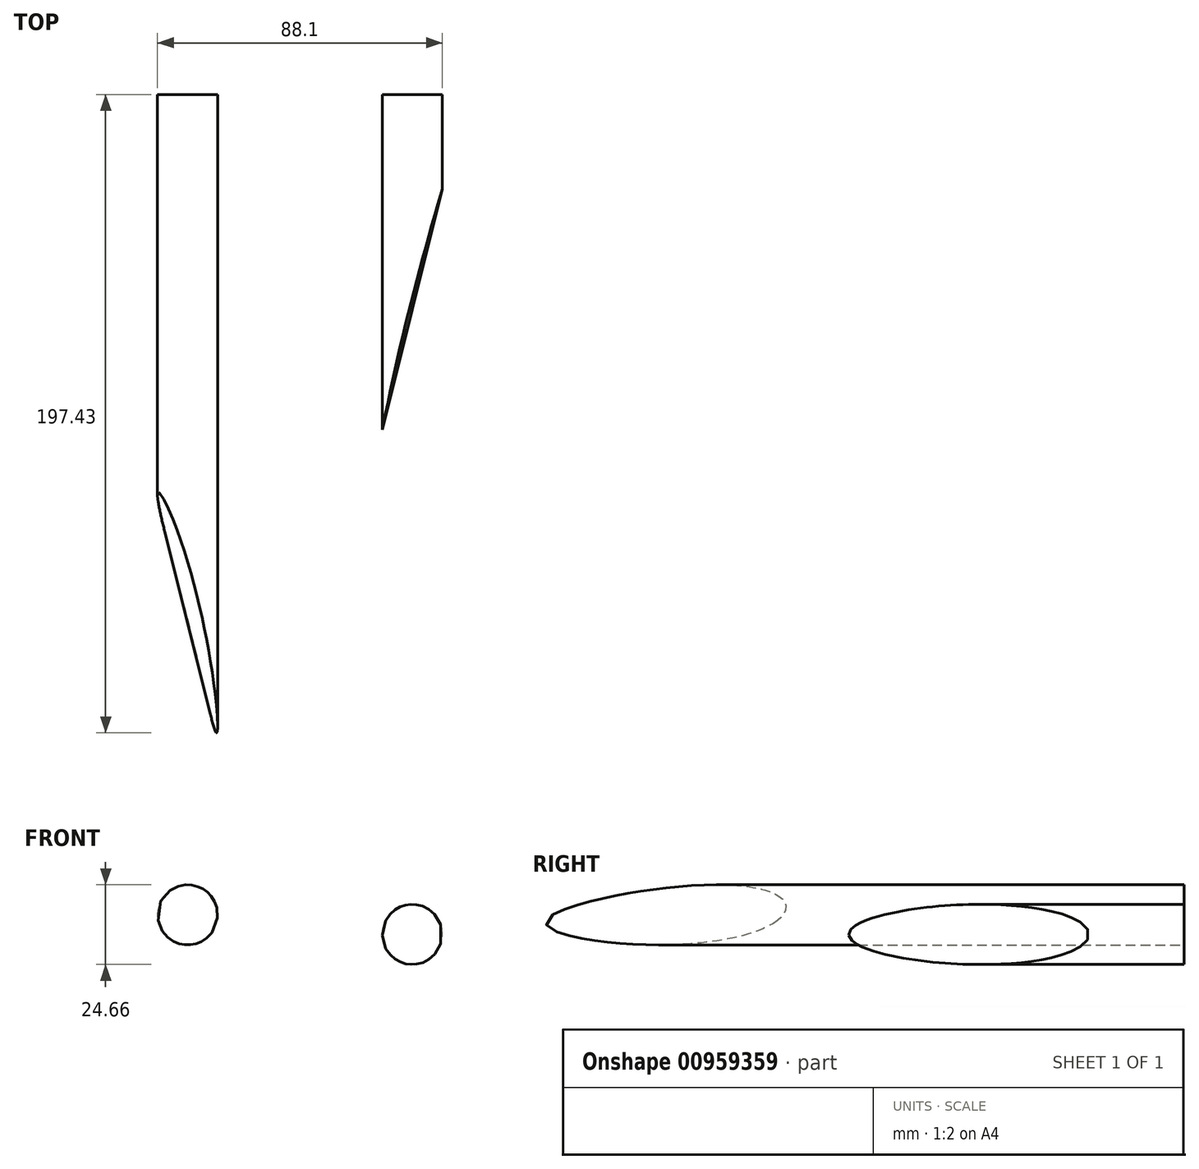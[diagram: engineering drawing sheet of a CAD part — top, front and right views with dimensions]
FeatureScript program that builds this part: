
annotation { "Feature Type Name" : "Feature", "Feature Type Description" : "" }
export const myFeature = defineFeature(function(context is Context, id is Id, definition is map)
    precondition{}
    {
        {
            var Q0;
            Q0=qCreatedBy(makeId("Front.planeOp"),FACE);
            var sketch = newSketch(context, id + "F0", { "sketchPlane" : qUnion([Q0])});
            skCircle(sketch, "E0", {"center": v(0, 0) * mm, "radius": 63.5 * mm});
            skLineSegment(sketch, "E1.0", {"start": v(40.6, 23.44) * mm, "end": v(40.6, -23.44) * mm, "construction": true});
            skLineSegment(sketch, "E1.1", {"start": v(40.6, -23.44) * mm, "end": v(0, -46.87) * mm, "construction": true});
            skLineSegment(sketch, "E1.2", {"start": v(0, -46.87) * mm, "end": v(-40.6, -23.44) * mm, "construction": true});
            skLineSegment(sketch, "E1.3", {"start": v(-40.6, -23.44) * mm, "end": v(-40.6, 23.44) * mm, "construction": true});
            skLineSegment(sketch, "E1.4", {"start": v(-40.6, 23.44) * mm, "end": v(0, 46.87) * mm, "construction": true});
            skLineSegment(sketch, "E1.5", {"start": v(0, 46.87) * mm, "end": v(40.6, 23.44) * mm, "construction": true});
            skPoint(sketch, "E1.0.midPoint", {"position": v(40.6, 0) * mm});
            skCircle(sketch, "E2", {"center": v(0, 0) * mm, "radius": 56.17 * mm, "construction": true});
            skCircle(sketch, "E3", {"center": v(0, 46.87) * mm, "radius": 9.3 * mm});
            skCircle(sketch, "E4", {"center": v(-40.6, 23.44) * mm, "radius": 9.3 * mm});
            skCircle(sketch, "E5", {"center": v(-40.6, -23.44) * mm, "radius": 9.3 * mm});
            skCircle(sketch, "E6", {"center": v(0, -46.87) * mm, "radius": 9.3 * mm});
            skCircle(sketch, "E7", {"center": v(40.6, -23.44) * mm, "radius": 9.3 * mm});
            skCircle(sketch, "E8", {"center": v(40.6, 23.44) * mm, "radius": 9.3 * mm});
            skCircle(sketch, "E9", {"center": v(-23.44, 40.6) * mm, "radius": 9.3 * mm});
            skCircle(sketch, "E10", {"center": v(-46.87, 0) * mm, "radius": 9.3 * mm});
            skCircle(sketch, "E11", {"center": v(-23.44, -40.6) * mm, "radius": 9.3 * mm});
            skLineSegment(sketch, "E12", {"start": v(-40.6, 23.44) * mm, "end": v(40.6, 23.44) * mm, "construction": true});
            skLineSegment(sketch, "E13", {"start": v(-40.6, -23.44) * mm, "end": v(40.6, -23.44) * mm, "construction": true});
            skCircle(sketch, "E14", {"center": v(23.44, 40.6) * mm, "radius": 9.3 * mm});
            skCircle(sketch, "E15", {"center": v(23.44, -40.6) * mm, "radius": 9.3 * mm});
            skCircle(sketch, "E16.MirrorC", {"center": v(46.87, 0) * mm, "radius": 9.3 * mm});
            skLineSegment(sketch, "E17", {"start": v(0, 0) * mm, "end": v(-28.09, 48.64) * mm});
            skLineSegment(sketch, "E18", {"start": v(0, 0) * mm, "end": v(28.09, -48.64) * mm});
            skLineSegment(sketch, "E19", {"start": v(0, 0) * mm, "end": v(-28.09, -48.64) * mm});
            skLineSegment(sketch, "E20", {"start": v(0, 0) * mm, "end": v(28.09, 48.64) * mm});
            skCircle(sketch, "E21", {"center": v(-22.64, 6.07) * mm, "radius": 9.3 * mm});
            skLineSegment(sketch, "E22.anchor1", {"start": v(0, 0) * mm, "end": v(-22.64, 6.07) * mm, "construction": true});
            skLineSegment(sketch, "E22.anchor2", {"start": v(0, 0) * mm, "end": v(-22.64, 6.07) * mm, "construction": true});
            skCircle(sketch, "E23.1.0", {"center": v(-16.57, -16.57) * mm, "radius": 9.3 * mm});
            skCircle(sketch, "E23.2.0", {"center": v(6.07, -22.64) * mm, "radius": 9.3 * mm});
            skCircle(sketch, "E24.1.3.0", {"center": v(22.64, -6.07) * mm, "radius": 9.3 * mm});
            skCircle(sketch, "E24.1.4.0", {"center": v(16.57, 16.57) * mm, "radius": 9.3 * mm});
            skCircle(sketch, "E24.1.5.0", {"center": v(-6.07, 22.64) * mm, "radius": 9.3 * mm});
            skSolve(sketch);
        }
        {
            var Q0;
            Q0=qCreatedBy(makeId("Right.planeOp"),FACE);
            var sketch = newSketch(context, id + "F1", { "sketchPlane" : qUnion([Q0])});
            skLineSegment(sketch, "E25", {"start": v(0, 0) * mm, "end": v(-254, 0) * mm});
            skLineSegment(sketch, "E26", {"start": v(0, 0) * mm, "end": v(0, 63.5) * mm});
            skLineSegment(sketch, "E27", {"start": v(-254, 0) * mm, "end": v(0, 63.5) * mm});
            skSolve(sketch);
        }
        {
            var Q0;
            Q0=makeQuery(id+"F1.imprint","IMPRINT",FACE,{"disambiguationData":[TD([[makeQuery(id+"F1.imprint","IMPRINT",EDGE,{"derivedFrom":sQuery(id+"F1.wireOp",EDGE,"E25")}),-1.0]])]});
            var Q1;
            Q1=sQuery(id+"F1.wireOp",EDGE,"E25");
            revolve(context, id + "F2", {"surfaceOperationType" : NewSurfaceOperationType.NEW, "entities" : qUnion([Q0]), "axis" : qUnion([Q1]), "revolveType" : RevolveType.FULL});
        }
        {
            var Q0;
            Q0=makeQuery(id+"F0.imprint","IMPRINT",FACE,{"disambiguationData":[TD([[makeQuery(id+"F0.imprint","IMPRINT",EDGE,{"derivedFrom":sQuery(id+"F0.wireOp",EDGE,"E10")}),1.0]])]});
            var Q1;
            Q1=makeQuery(id+"F0.imprint","IMPRINT",FACE,{"disambiguationData":[TD([[makeQuery(id+"F0.imprint","IMPRINT",EDGE,{"derivedFrom":sQuery(id+"F0.wireOp",EDGE,"E5")}),1.0]])]});
            var Q2;
            {var subQ0=sQuery(id+"F0.wireOp",EDGE,"E19");var subQ1=sQuery(id+"F0.wireOp",EDGE,"E11");var subQ2=makeQuery(id+"F0.imprint","INTERSECT",VERTEX,{"disambiguationData":[OD(0.0)],"derivedFrom":[subQ1,subQ0]});Q2=makeQuery(id+"F0.imprint","IMPRINT",FACE,{"disambiguationData":[TD([[makeQuery(id+"F0.imprint","IMPRINT",EDGE,{"disambiguationData":[TD([[subQ2,1.0]])],"derivedFrom":subQ1}),1.0]])]});}
            var Q3;
            {var subQ0=sQuery(id+"F0.wireOp",EDGE,"E19");var subQ1=sQuery(id+"F0.wireOp",EDGE,"E11");var subQ2=makeQuery(id+"F0.imprint","INTERSECT",VERTEX,{"disambiguationData":[OD(0.0)],"derivedFrom":[subQ1,subQ0]});Q3=makeQuery(id+"F0.imprint","IMPRINT",FACE,{"disambiguationData":[TD([[makeQuery(id+"F0.imprint","IMPRINT",EDGE,{"disambiguationData":[TD([[subQ2,-1.0]])],"derivedFrom":subQ1}),1.0]])]});}
            var Q4;
            Q4=makeQuery(id+"F0.imprint","IMPRINT",FACE,{"disambiguationData":[TD([[makeQuery(id+"F0.imprint","IMPRINT",EDGE,{"derivedFrom":sQuery(id+"F0.wireOp",EDGE,"E6")}),1.0]])]});
            var Q5;
            {var subQ0=sQuery(id+"F0.wireOp",EDGE,"E18");var subQ1=sQuery(id+"F0.wireOp",EDGE,"E15");var subQ2=makeQuery(id+"F0.imprint","INTERSECT",VERTEX,{"disambiguationData":[OD(0.0)],"derivedFrom":[subQ1,subQ0]});Q5=makeQuery(id+"F0.imprint","IMPRINT",FACE,{"disambiguationData":[TD([[makeQuery(id+"F0.imprint","IMPRINT",EDGE,{"disambiguationData":[TD([[subQ2,-1.0]])],"derivedFrom":subQ1}),1.0]])]});}
            var Q6;
            {var subQ0=sQuery(id+"F0.wireOp",EDGE,"E18");var subQ1=sQuery(id+"F0.wireOp",EDGE,"E15");var subQ2=makeQuery(id+"F0.imprint","INTERSECT",VERTEX,{"disambiguationData":[OD(0.0)],"derivedFrom":[subQ1,subQ0]});Q6=makeQuery(id+"F0.imprint","IMPRINT",FACE,{"disambiguationData":[TD([[makeQuery(id+"F0.imprint","IMPRINT",EDGE,{"disambiguationData":[TD([[subQ2,1.0]])],"derivedFrom":subQ1}),1.0]])]});}
            var Q7;
            Q7=makeQuery(id+"F0.imprint","IMPRINT",FACE,{"disambiguationData":[TD([[makeQuery(id+"F0.imprint","IMPRINT",EDGE,{"derivedFrom":sQuery(id+"F0.wireOp",EDGE,"E7")}),1.0]])]});
            var Q8;
            Q8=makeQuery(id+"F0.imprint","IMPRINT",FACE,{"disambiguationData":[TD([[makeQuery(id+"F0.imprint","IMPRINT",EDGE,{"derivedFrom":sQuery(id+"F0.wireOp",EDGE,"E16.MirrorC")}),-1.0]])]});
            var Q9;
            Q9=makeQuery(id+"F0.imprint","IMPRINT",FACE,{"disambiguationData":[TD([[makeQuery(id+"F0.imprint","IMPRINT",EDGE,{"derivedFrom":sQuery(id+"F0.wireOp",EDGE,"E8")}),1.0]])]});
            var Q10;
            {var subQ0=sQuery(id+"F0.wireOp",EDGE,"E20");var subQ1=sQuery(id+"F0.wireOp",EDGE,"E14");var subQ2=makeQuery(id+"F0.imprint","INTERSECT",VERTEX,{"disambiguationData":[OD(0.0)],"derivedFrom":[subQ1,subQ0]});Q10=makeQuery(id+"F0.imprint","IMPRINT",FACE,{"disambiguationData":[TD([[makeQuery(id+"F0.imprint","IMPRINT",EDGE,{"disambiguationData":[TD([[subQ2,1.0]])],"derivedFrom":subQ1}),1.0]])]});}
            var Q11;
            {var subQ0=sQuery(id+"F0.wireOp",EDGE,"E20");var subQ1=sQuery(id+"F0.wireOp",EDGE,"E14");var subQ2=makeQuery(id+"F0.imprint","INTERSECT",VERTEX,{"disambiguationData":[OD(0.0)],"derivedFrom":[subQ1,subQ0]});Q11=makeQuery(id+"F0.imprint","IMPRINT",FACE,{"disambiguationData":[TD([[makeQuery(id+"F0.imprint","IMPRINT",EDGE,{"disambiguationData":[TD([[subQ2,-1.0]])],"derivedFrom":subQ1}),1.0]])]});}
            var Q12;
            Q12=makeQuery(id+"F0.imprint","IMPRINT",FACE,{"disambiguationData":[TD([[makeQuery(id+"F0.imprint","IMPRINT",EDGE,{"derivedFrom":sQuery(id+"F0.wireOp",EDGE,"E3")}),1.0]])]});
            var Q13;
            {var subQ0=sQuery(id+"F0.wireOp",EDGE,"E17");var subQ1=sQuery(id+"F0.wireOp",EDGE,"E9");var subQ2=makeQuery(id+"F0.imprint","INTERSECT",VERTEX,{"disambiguationData":[OD(0.0)],"derivedFrom":[subQ1,subQ0]});Q13=makeQuery(id+"F0.imprint","IMPRINT",FACE,{"disambiguationData":[TD([[makeQuery(id+"F0.imprint","IMPRINT",EDGE,{"disambiguationData":[TD([[subQ2,-1.0]])],"derivedFrom":subQ1}),1.0]])]});}
            var Q14;
            {var subQ0=sQuery(id+"F0.wireOp",EDGE,"E17");var subQ1=sQuery(id+"F0.wireOp",EDGE,"E9");var subQ2=makeQuery(id+"F0.imprint","INTERSECT",VERTEX,{"disambiguationData":[OD(0.0)],"derivedFrom":[subQ1,subQ0]});Q14=makeQuery(id+"F0.imprint","IMPRINT",FACE,{"disambiguationData":[TD([[makeQuery(id+"F0.imprint","IMPRINT",EDGE,{"disambiguationData":[TD([[subQ2,1.0]])],"derivedFrom":subQ1}),1.0]])]});}
            var Q15;
            Q15=makeQuery(id+"F0.imprint","IMPRINT",FACE,{"disambiguationData":[TD([[makeQuery(id+"F0.imprint","IMPRINT",EDGE,{"derivedFrom":sQuery(id+"F0.wireOp",EDGE,"E4")}),1.0]])]});
            var Q16;
            Q16=makeQuery(id+"F0.imprint","IMPRINT",FACE,{"disambiguationData":[TD([[makeQuery(id+"F0.imprint","IMPRINT",EDGE,{"derivedFrom":sQuery(id+"F0.wireOp",EDGE,"E21")}),1.0]])]});
            var Q17;
            {var subQ0=sQuery(id+"F0.wireOp",EDGE,"E23.1.0");var subQ1=sQuery(id+"F0.wireOp",EDGE,"E19");var subQ2=makeQuery(id+"F0.imprint","INTERSECT",VERTEX,{"disambiguationData":[OD(0.0)],"derivedFrom":[subQ1,subQ0]});Q17=makeQuery(id+"F0.imprint","IMPRINT",FACE,{"disambiguationData":[TD([[makeQuery(id+"F0.imprint","IMPRINT",EDGE,{"disambiguationData":[TD([[subQ2,1.0]])],"derivedFrom":subQ1}),-1.0]])]});}
            var Q18;
            {var subQ0=sQuery(id+"F0.wireOp",EDGE,"E23.1.0");var subQ1=sQuery(id+"F0.wireOp",EDGE,"E19");var subQ2=makeQuery(id+"F0.imprint","INTERSECT",VERTEX,{"disambiguationData":[OD(0.0)],"derivedFrom":[subQ1,subQ0]});Q18=makeQuery(id+"F0.imprint","IMPRINT",FACE,{"disambiguationData":[TD([[makeQuery(id+"F0.imprint","IMPRINT",EDGE,{"disambiguationData":[TD([[subQ2,1.0]])],"derivedFrom":subQ1}),1.0]])]});}
            var Q19;
            {var subQ0=sQuery(id+"F0.wireOp",EDGE,"E23.2.0");var subQ1=sQuery(id+"F0.wireOp",EDGE,"E18");var subQ2=makeQuery(id+"F0.imprint","INTERSECT",VERTEX,{"disambiguationData":[OD(0.0)],"derivedFrom":[subQ1,subQ0]});Q19=makeQuery(id+"F0.imprint","IMPRINT",FACE,{"disambiguationData":[TD([[makeQuery(id+"F0.imprint","IMPRINT",EDGE,{"disambiguationData":[TD([[subQ2,-1.0]])],"derivedFrom":subQ1}),-1.0]])]});}
            var Q20;
            {var subQ0=sQuery(id+"F0.wireOp",EDGE,"E23.2.0");var subQ1=sQuery(id+"F0.wireOp",EDGE,"E18");var subQ2=makeQuery(id+"F0.imprint","INTERSECT",VERTEX,{"disambiguationData":[OD(0.0)],"derivedFrom":[subQ1,subQ0]});Q20=makeQuery(id+"F0.imprint","IMPRINT",FACE,{"disambiguationData":[TD([[makeQuery(id+"F0.imprint","IMPRINT",EDGE,{"disambiguationData":[TD([[subQ2,-1.0]])],"derivedFrom":subQ1}),1.0]])]});}
            var Q21;
            Q21=makeQuery(id+"F0.imprint","IMPRINT",FACE,{"disambiguationData":[TD([[makeQuery(id+"F0.imprint","IMPRINT",EDGE,{"derivedFrom":sQuery(id+"F0.wireOp",EDGE,"E24.1.3.0")}),1.0]])]});
            var Q22;
            {var subQ0=sQuery(id+"F0.wireOp",EDGE,"E24.1.4.0");var subQ1=sQuery(id+"F0.wireOp",EDGE,"E20");var subQ2=makeQuery(id+"F0.imprint","INTERSECT",VERTEX,{"disambiguationData":[OD(0.0)],"derivedFrom":[subQ1,subQ0]});Q22=makeQuery(id+"F0.imprint","IMPRINT",FACE,{"disambiguationData":[TD([[makeQuery(id+"F0.imprint","IMPRINT",EDGE,{"disambiguationData":[TD([[subQ2,-1.0]])],"derivedFrom":subQ1}),-1.0]])]});}
            var Q23;
            {var subQ0=sQuery(id+"F0.wireOp",EDGE,"E24.1.4.0");var subQ1=sQuery(id+"F0.wireOp",EDGE,"E20");var subQ2=makeQuery(id+"F0.imprint","INTERSECT",VERTEX,{"disambiguationData":[OD(0.0)],"derivedFrom":[subQ1,subQ0]});Q23=makeQuery(id+"F0.imprint","IMPRINT",FACE,{"disambiguationData":[TD([[makeQuery(id+"F0.imprint","IMPRINT",EDGE,{"disambiguationData":[TD([[subQ2,-1.0]])],"derivedFrom":subQ1}),1.0]])]});}
            var Q24;
            {var subQ0=sQuery(id+"F0.wireOp",EDGE,"E24.1.5.0");var subQ1=sQuery(id+"F0.wireOp",EDGE,"E17");var subQ2=makeQuery(id+"F0.imprint","INTERSECT",VERTEX,{"disambiguationData":[OD(0.0)],"derivedFrom":[subQ1,subQ0]});Q24=makeQuery(id+"F0.imprint","IMPRINT",FACE,{"disambiguationData":[TD([[makeQuery(id+"F0.imprint","IMPRINT",EDGE,{"disambiguationData":[TD([[subQ2,1.0]])],"derivedFrom":subQ1}),-1.0]])]});}
            var Q25;
            {var subQ0=sQuery(id+"F0.wireOp",EDGE,"E24.1.5.0");var subQ1=sQuery(id+"F0.wireOp",EDGE,"E17");var subQ2=makeQuery(id+"F0.imprint","INTERSECT",VERTEX,{"disambiguationData":[OD(0.0)],"derivedFrom":[subQ1,subQ0]});Q25=makeQuery(id+"F0.imprint","IMPRINT",FACE,{"disambiguationData":[TD([[makeQuery(id+"F0.imprint","IMPRINT",EDGE,{"disambiguationData":[TD([[subQ2,1.0]])],"derivedFrom":subQ1}),1.0]])]});}
            extrude(context, id + "F3", {"entities" : qUnion([Q0, Q1, Q2, Q3, Q4, Q5, Q6, Q7, Q8, Q9, Q10, Q11, Q12, Q13, Q14, Q15, Q16, Q17, Q18, Q19, Q20, Q21, Q22, Q23, Q24, Q25]), "depth" : 254 * mm, "offsetDistance" : 25.4 * mm});
        }
        {
            var Q0;
            Q0=makeQuery(id+"F3.opExtrude","SWEPT_BODY",BODY,{"disambiguationData":[OSD([sQuery(id+"F0.wireOp",EDGE,"E3")])]});
            var Q1;
            Q1=makeQuery(id+"F3.opExtrude","SWEPT_BODY",BODY,{"disambiguationData":[OSD([sQuery(id+"F0.wireOp",EDGE,"E24.1.4.0")])]});
            var Q2;
            Q2=makeQuery(id+"F3.opExtrude","SWEPT_BODY",BODY,{"disambiguationData":[OSD([sQuery(id+"F0.wireOp",EDGE,"E23.2.0")])]});
            var Q3;
            Q3=makeQuery(id+"F3.opExtrude","SWEPT_BODY",BODY,{"disambiguationData":[OSD([sQuery(id+"F0.wireOp",EDGE,"E21")])]});
            var Q4;
            Q4=makeQuery(id+"F3.opExtrude","SWEPT_BODY",BODY,{"disambiguationData":[OSD([sQuery(id+"F0.wireOp",EDGE,"E16.MirrorC")])]});
            var Q5;
            Q5=makeQuery(id+"F3.opExtrude","SWEPT_BODY",BODY,{"disambiguationData":[OSD([sQuery(id+"F0.wireOp",EDGE,"E11")])]});
            var Q6;
            Q6=makeQuery(id+"F3.opExtrude","SWEPT_BODY",BODY,{"disambiguationData":[OSD([sQuery(id+"F0.wireOp",EDGE,"E10")])]});
            var Q7;
            Q7=makeQuery(id+"F3.opExtrude","SWEPT_BODY",BODY,{"disambiguationData":[OSD([sQuery(id+"F0.wireOp",EDGE,"E9")])]});
            var Q8;
            Q8=makeQuery(id+"F3.opExtrude","SWEPT_BODY",BODY,{"disambiguationData":[OSD([sQuery(id+"F0.wireOp",EDGE,"E8")])]});
            var Q9;
            Q9=makeQuery(id+"F3.opExtrude","SWEPT_BODY",BODY,{"disambiguationData":[OSD([sQuery(id+"F0.wireOp",EDGE,"E7")])]});
            var Q10;
            Q10=makeQuery(id+"F3.opExtrude","SWEPT_BODY",BODY,{"disambiguationData":[OSD([sQuery(id+"F0.wireOp",EDGE,"E6")])]});
            var Q11;
            Q11=makeQuery(id+"F3.opExtrude","SWEPT_BODY",BODY,{"disambiguationData":[OSD([sQuery(id+"F0.wireOp",EDGE,"E5")])]});
            var Q12;
            Q12=makeQuery(id+"F3.opExtrude","SWEPT_BODY",BODY,{"disambiguationData":[OSD([sQuery(id+"F0.wireOp",EDGE,"E4")])]});
            var Q13;
            Q13=makeQuery(id+"F3.opExtrude","SWEPT_BODY",BODY,{"disambiguationData":[OSD([sQuery(id+"F0.wireOp",EDGE,"E15")])]});
            var Q14;
            Q14=makeQuery(id+"F3.opExtrude","SWEPT_BODY",BODY,{"disambiguationData":[OSD([sQuery(id+"F0.wireOp",EDGE,"E23.1.0")])]});
            var Q15;
            Q15=makeQuery(id+"F3.opExtrude","SWEPT_BODY",BODY,{"disambiguationData":[OSD([sQuery(id+"F0.wireOp",EDGE,"E24.1.3.0")])]});
            var Q16;
            Q16=makeQuery(id+"F3.opExtrude","SWEPT_BODY",BODY,{"disambiguationData":[OSD([sQuery(id+"F0.wireOp",EDGE,"E24.1.5.0")])]});
            var Q17;
            Q17=makeQuery(id+"F3.opExtrude","SWEPT_BODY",BODY,{"disambiguationData":[OSD([sQuery(id+"F0.wireOp",EDGE,"E14")])]});
            var Q18;
            Q18=makeQuery(id+"F2.opRevolve","SWEPT_BODY",BODY,{"disambiguationData":[OSD([sQuery(id+"F1.wireOp",EDGE,"E25"),sQuery(id+"F1.wireOp",EDGE,"E26"),sQuery(id+"F1.wireOp",EDGE,"E27")])]});
            booleanBodies(context, id + "F4", {"operationType" : BooleanOperationType.SUBTRACTION, "tools" : qUnion([Q0, Q1, Q2, Q3, Q4, Q5, Q6, Q7, Q8, Q9, Q10, Q11, Q12, Q13, Q14, Q15, Q16, Q17]), "targets" : qUnion([Q18])});
        }
    });
